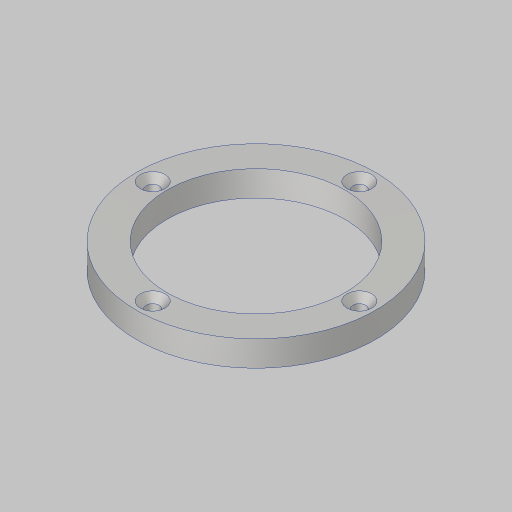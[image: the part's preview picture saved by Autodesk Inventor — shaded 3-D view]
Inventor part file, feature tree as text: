
AUTODESK INVENTOR PART (.ipt)
format: ipt  version: 2023.5 (Build 275446000, 446)  size: 127,488 bytes
history: native  units: in
note: dims shown in document units (in); Inventor stores cm internally (conversion verified against a paired STEP export)
features: sketch x2, extrude x1, hole x1, projected_geometry x1
ambient origin geometry x8: Origin, YZ Plane, XZ Plane, XY Plane, X Axis, Y Axis, Z Axis, Center Point
bodies: Solid1 (feature_tree)
feature tree (5):
  extrude  "Extrusion1"  Depth=4.7244in
  hole  "Hole1"  [1 undecoded]
  sketch  "Sketch1"  dims[d0=2.7559in d1=4.7244in]
  sketch  "Sketch2"  dims[d2=0.3937in d3=0.0in d5=0.201in d6=0.75in d7=0.385in d8=0.25in d9=0.5635in d10=1.0in d11=0.8108in d15=0.4724in d16=1.5748in d18=360.0deg d20=3.2in d21=1.5748in d23=360.0deg]
  projected_geometry  "Project Cut Edges1"
note: 1 required parameter value undecoded (feature->parameter linkage not recoverable at this tier; creation-order binding heuristic only, values carry confidence <= 0.55)
